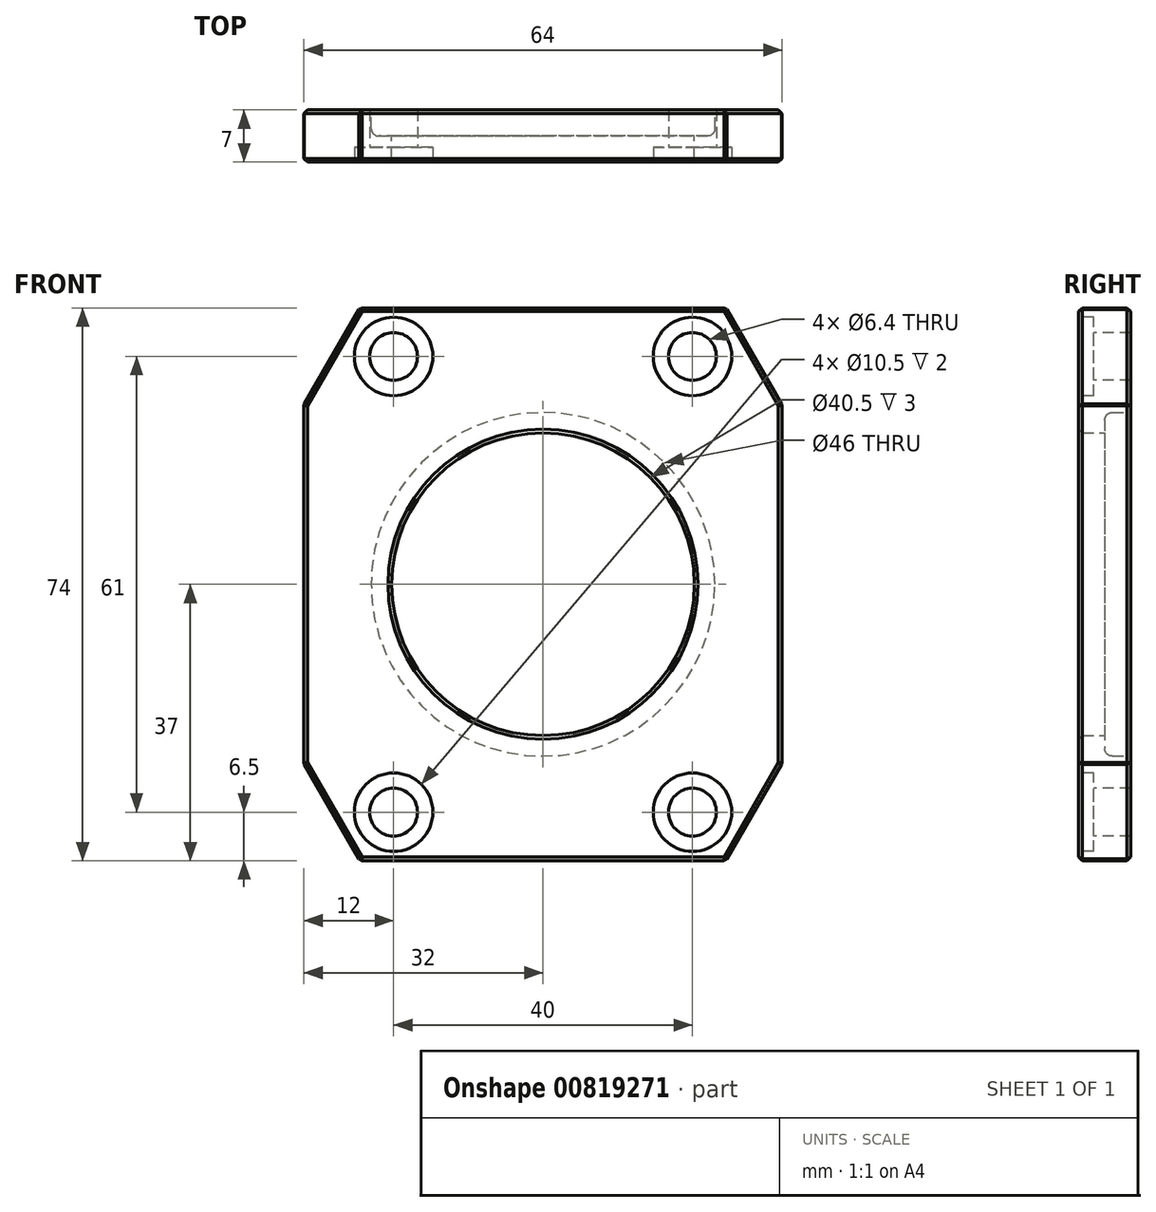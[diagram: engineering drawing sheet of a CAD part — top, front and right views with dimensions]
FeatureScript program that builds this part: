
annotation { "Feature Type Name" : "Feature", "Feature Type Description" : "" }
export const myFeature = defineFeature(function(context is Context, id is Id, definition is map)
    precondition{}
    {
        {
            var Q0;
            Q0=qCreatedBy(makeId("Front.planeOp"),FACE);
            var sketch = newSketch(context, id + "F0", { "sketchPlane" : qUnion([Q0])});
            skLineSegment(sketch, "E0", {"start": v(0, 37) * mm, "end": v(-24.5, 37) * mm});
            skLineSegment(sketch, "E1", {"start": v(-24.5, 37) * mm, "end": v(-32, 24) * mm});
            skLineSegment(sketch, "E2", {"start": v(-32, 24) * mm, "end": v(-32, 0) * mm});
            skLineSegment(sketch, "E3.MirrorCS", {"start": v(0, 37) * mm, "end": v(24.5, 37) * mm});
            skLineSegment(sketch, "E4.MirrorCS", {"start": v(24.5, 37) * mm, "end": v(32, 24) * mm});
            skLineSegment(sketch, "E5.MirrorCS", {"start": v(32, 24) * mm, "end": v(32, 0) * mm});
            skLineSegment(sketch, "E6.MirrorCS", {"start": v(-32, -24) * mm, "end": v(-32, 0) * mm});
            skLineSegment(sketch, "E7.MirrorCS", {"start": v(-24.5, -37) * mm, "end": v(-32, -24) * mm});
            skLineSegment(sketch, "E8.MirrorCS", {"start": v(0, -37) * mm, "end": v(-24.5, -37) * mm});
            skLineSegment(sketch, "E9.MirrorCS", {"start": v(0, -37) * mm, "end": v(24.5, -37) * mm});
            skLineSegment(sketch, "E10.MirrorCS", {"start": v(24.5, -37) * mm, "end": v(32, -24) * mm});
            skLineSegment(sketch, "E11.MirrorCS", {"start": v(32, -24) * mm, "end": v(32, 0) * mm});
            skSolve(sketch);
        }
        {
            var Q0;
            Q0=makeQuery(id+"F0.imprint","IMPRINT",FACE,{"disambiguationData":[TD([[makeQuery(id+"F0.imprint","IMPRINT",EDGE,{"derivedFrom":sQuery(id+"F0.wireOp",EDGE,"E0")}),1.0]])]});
            extrude(context, id + "F1", {"entities" : qUnion([Q0]), "depth" : 7 * mm, "offsetDistance" : 25 * mm});
        }
        {
            var Q0;
            Q0=makeQuery(id+"F1.opExtrude","CAP_FACE",FACE,{"disambiguationData":[OSD([sQuery(id+"F0.wireOp",EDGE,"E0"),sQuery(id+"F0.wireOp",EDGE,"E1"),sQuery(id+"F0.wireOp",EDGE,"E2"),sQuery(id+"F0.wireOp",EDGE,"E3.MirrorCS"),sQuery(id+"F0.wireOp",EDGE,"E4.MirrorCS"),sQuery(id+"F0.wireOp",EDGE,"E5.MirrorCS"),sQuery(id+"F0.wireOp",EDGE,"E6.MirrorCS"),sQuery(id+"F0.wireOp",EDGE,"E7.MirrorCS"),sQuery(id+"F0.wireOp",EDGE,"E8.MirrorCS"),sQuery(id+"F0.wireOp",EDGE,"E9.MirrorCS"),sQuery(id+"F0.wireOp",EDGE,"E10.MirrorCS"),sQuery(id+"F0.wireOp",EDGE,"E11.MirrorCS")])],"isStart":false});
            var sketch = newSketch(context, id + "F2", { "sketchPlane" : qUnion([Q0])});
            skPoint(sketch, "E12", {"position": v(20, 30.5) * mm});
            skPoint(sketch, "E13.MirrorP", {"position": v(-20, 30.5) * mm});
            skPoint(sketch, "E14.MirrorP", {"position": v(-20, -30.5) * mm});
            skPoint(sketch, "E15.MirrorP", {"position": v(20, -30.5) * mm});
            skSolve(sketch);
        }
        {
            var Q0;
            Q0=sQuery(id+"F2.wireOp",VERTEX,"E12");
            var Q1;
            Q1=sQuery(id+"F2.wireOp",VERTEX,"E13.MirrorP");
            var Q2;
            Q2=sQuery(id+"F2.wireOp",VERTEX,"E14.MirrorP");
            var Q3;
            Q3=sQuery(id+"F2.wireOp",VERTEX,"E15.MirrorP");
            var Q4;
            Q4=makeQuery(id+"F1.opExtrude","SWEPT_BODY",BODY,{"disambiguationData":[OSD([sQuery(id+"F0.wireOp",EDGE,"E0"),sQuery(id+"F0.wireOp",EDGE,"E1"),sQuery(id+"F0.wireOp",EDGE,"E2"),sQuery(id+"F0.wireOp",EDGE,"E3.MirrorCS"),sQuery(id+"F0.wireOp",EDGE,"E4.MirrorCS"),sQuery(id+"F0.wireOp",EDGE,"E5.MirrorCS"),sQuery(id+"F0.wireOp",EDGE,"E6.MirrorCS"),sQuery(id+"F0.wireOp",EDGE,"E7.MirrorCS"),sQuery(id+"F0.wireOp",EDGE,"E8.MirrorCS"),sQuery(id+"F0.wireOp",EDGE,"E9.MirrorCS"),sQuery(id+"F0.wireOp",EDGE,"E10.MirrorCS"),sQuery(id+"F0.wireOp",EDGE,"E11.MirrorCS")])]});
            hole(context, id + "F3", {"style" : HoleStyle.C_BORE, "endStyle" : HoleEndStyle.THROUGH, "holeDiameter" : 6.4 * mm, "cBoreDiameter" : 10.5 * mm, "cBoreDepth" : 2 * mm, "majorDiameter" : 8 * mm, "isTappedThrough" : true, "tappedDepth" : 36.25 * mm, "tapClearance" : 3, "locations" : qUnion([Q0, Q1, Q2, Q3]), "scope" : qUnion([Q4])});
        }
        {
            var Q0;
            Q0=makeQuery(id+"F1.opExtrude","CAP_FACE",FACE,{"disambiguationData":[OSD([sQuery(id+"F0.wireOp",EDGE,"E0"),sQuery(id+"F0.wireOp",EDGE,"E1"),sQuery(id+"F0.wireOp",EDGE,"E2"),sQuery(id+"F0.wireOp",EDGE,"E3.MirrorCS"),sQuery(id+"F0.wireOp",EDGE,"E4.MirrorCS"),sQuery(id+"F0.wireOp",EDGE,"E5.MirrorCS"),sQuery(id+"F0.wireOp",EDGE,"E6.MirrorCS"),sQuery(id+"F0.wireOp",EDGE,"E7.MirrorCS"),sQuery(id+"F0.wireOp",EDGE,"E8.MirrorCS"),sQuery(id+"F0.wireOp",EDGE,"E9.MirrorCS"),sQuery(id+"F0.wireOp",EDGE,"E10.MirrorCS"),sQuery(id+"F0.wireOp",EDGE,"E11.MirrorCS")])],"isStart":true});
            var sketch = newSketch(context, id + "F4", { "sketchPlane" : qUnion([Q0])});
            skCircle(sketch, "E16", {"center": v(0, 0) * mm, "radius": 20.25 * mm});
            skCircle(sketch, "E17", {"center": v(0, 0) * mm, "radius": 23 * mm});
            skSolve(sketch);
        }
        {
            var Q0;
            Q0=makeQuery(id+"F4.imprint","IMPRINT",FACE,{"disambiguationData":[TD([[makeQuery(id+"F4.imprint","IMPRINT",EDGE,{"derivedFrom":sQuery(id+"F4.wireOp",EDGE,"E16")}),1.0]])]});
            extrude(context, id + "F5", {"entities" : qUnion([Q0]), "operationType" : NewBodyOperationType.REMOVE, "endBound" : BoundingType.THROUGH_ALL, "oppositeDirection" : true, "depth" : 25 * mm, "offsetDistance" : 25 * mm});
        }
        {
            var Q0;
            Q0=makeQuery(id+"F4.imprint","IMPRINT",FACE,{"disambiguationData":[TD([[makeQuery(id+"F4.imprint","IMPRINT",EDGE,{"derivedFrom":sQuery(id+"F4.wireOp",EDGE,"E16")}),-1.0]])]});
            extrude(context, id + "F6", {"entities" : qUnion([Q0]), "operationType" : NewBodyOperationType.REMOVE, "oppositeDirection" : true, "depth" : 3.5 * mm, "offsetDistance" : 25 * mm});
        }
        {
            var Q0;
            Q0=makeQuery(id+"F1.opExtrude","SWEPT_FACE",FACE,{"disambiguationData":[OSD([sQuery(id+"F0.wireOp",EDGE,"E8.MirrorCS"),sQuery(id+"F0.wireOp",EDGE,"E9.MirrorCS")])]});
            var Q1;
            Q1=makeQuery(id+"F1.opExtrude","SWEPT_FACE",FACE,{"disambiguationData":[OSD([sQuery(id+"F0.wireOp",EDGE,"E10.MirrorCS")])]});
            var Q2;
            Q2=makeQuery(id+"F1.opExtrude","SWEPT_FACE",FACE,{"disambiguationData":[OSD([sQuery(id+"F0.wireOp",EDGE,"E5.MirrorCS"),sQuery(id+"F0.wireOp",EDGE,"E11.MirrorCS")])]});
            var Q3;
            Q3=makeQuery(id+"F1.opExtrude","SWEPT_FACE",FACE,{"disambiguationData":[OSD([sQuery(id+"F0.wireOp",EDGE,"E0"),sQuery(id+"F0.wireOp",EDGE,"E3.MirrorCS")])]});
            var Q4;
            Q4=makeQuery(id+"F1.opExtrude","SWEPT_FACE",FACE,{"disambiguationData":[OSD([sQuery(id+"F0.wireOp",EDGE,"E4.MirrorCS")])]});
            var Q5;
            Q5=makeQuery(id+"F1.opExtrude","SWEPT_FACE",FACE,{"disambiguationData":[OSD([sQuery(id+"F0.wireOp",EDGE,"E1")])]});
            var Q6;
            Q6=makeQuery(id+"F1.opExtrude","SWEPT_FACE",FACE,{"disambiguationData":[OSD([sQuery(id+"F0.wireOp",EDGE,"E2"),sQuery(id+"F0.wireOp",EDGE,"E6.MirrorCS")])]});
            var Q7;
            Q7=makeQuery(id+"F1.opExtrude","SWEPT_FACE",FACE,{"disambiguationData":[OSD([sQuery(id+"F0.wireOp",EDGE,"E7.MirrorCS")])]});
            chamfer(context, id + "F7", {"entities" : qUnion([Q0, Q1, Q2, Q3, Q4, Q5, Q6, Q7]), "width" : 0.5 * mm, "tangentPropagation" : true});
        }
        {
            var Q0;
            Q0=makeQuery(id+"F6.boolean.opBoolean","COPY",EDGE,{"derivedFrom":makeQuery(id+"F6.opExtrude","CAP_EDGE",EDGE,{"disambiguationData":[OSD([sQuery(id+"F4.wireOp",EDGE,"E17")])],"isStart":true})});
            var Q1;
            Q1=makeQuery(id+"F5.boolean.opBoolean","INTERSECT",EDGE,{"derivedFrom":[makeQuery(id+"F1.opExtrude","CAP_FACE",FACE,{"disambiguationData":[OSD([sQuery(id+"F0.wireOp",EDGE,"E0"),sQuery(id+"F0.wireOp",EDGE,"E1"),sQuery(id+"F0.wireOp",EDGE,"E2"),sQuery(id+"F0.wireOp",EDGE,"E3.MirrorCS"),sQuery(id+"F0.wireOp",EDGE,"E4.MirrorCS"),sQuery(id+"F0.wireOp",EDGE,"E5.MirrorCS"),sQuery(id+"F0.wireOp",EDGE,"E6.MirrorCS"),sQuery(id+"F0.wireOp",EDGE,"E7.MirrorCS"),sQuery(id+"F0.wireOp",EDGE,"E8.MirrorCS"),sQuery(id+"F0.wireOp",EDGE,"E9.MirrorCS"),sQuery(id+"F0.wireOp",EDGE,"E10.MirrorCS"),sQuery(id+"F0.wireOp",EDGE,"E11.MirrorCS")])],"isStart":false}),makeQuery(id+"F5.opExtrude","SWEPT_FACE",FACE,{"disambiguationData":[OSD([sQuery(id+"F4.wireOp",EDGE,"E16")])]})]});
            chamfer(context, id + "F8", {"entities" : qUnion([Q0, Q1]), "width" : 0.5 * mm, "tangentPropagation" : true});
        }
        {
            var Q0;
            Q0=makeQuery(id+"F6.boolean.opBoolean","COPY",EDGE,{"derivedFrom":makeQuery(id+"F6.opExtrude","CAP_EDGE",EDGE,{"disambiguationData":[OSD([sQuery(id+"F4.wireOp",EDGE,"E16")])],"isStart":false})});
            var Q1;
            Q1=makeQuery(id+"F6.boolean.opBoolean","COPY",EDGE,{"derivedFrom":makeQuery(id+"F6.opExtrude","CAP_EDGE",EDGE,{"disambiguationData":[OSD([sQuery(id+"F4.wireOp",EDGE,"E17")])],"isStart":false})});
            fillet(context, id + "F9", {"entities" : qUnion([Q0, Q1]), "radius" : 1 * mm, "tangentPropagation" : true, "allowEdgeOverflow" : false});
        }
    });
